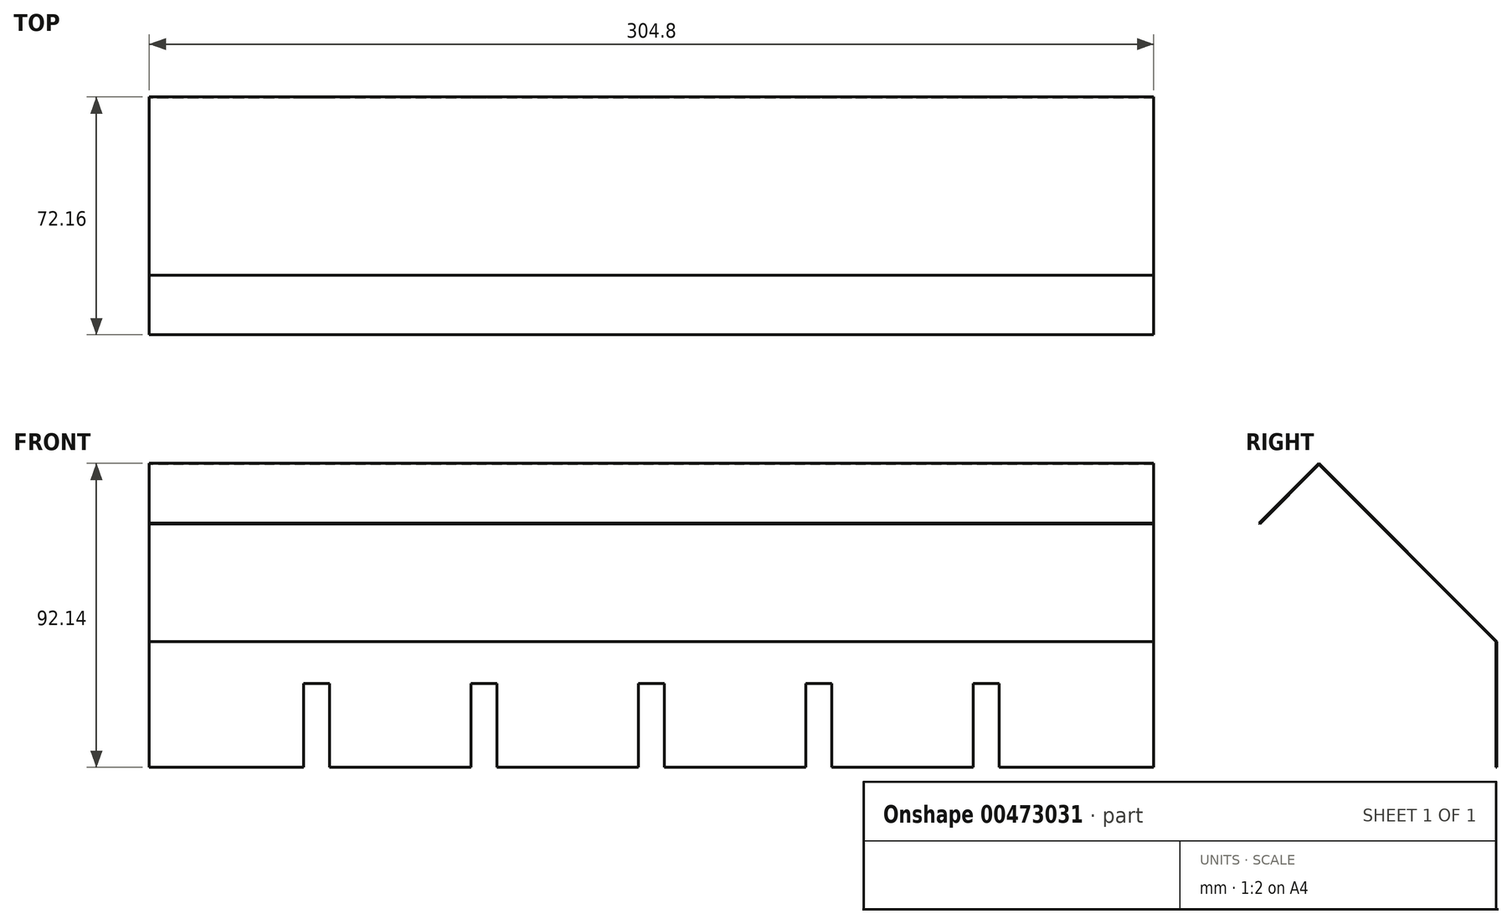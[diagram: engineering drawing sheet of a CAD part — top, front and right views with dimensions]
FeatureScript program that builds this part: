
annotation { "Feature Type Name" : "Feature", "Feature Type Description" : "" }
export const myFeature = defineFeature(function(context is Context, id is Id, definition is map)
    precondition{}
    {
        {
            var Q0;
            Q0=qCreatedBy(makeId("Front.planeOp"),FACE);
            var sketch = newSketch(context, id + "F0", { "sketchPlane" : qUnion([Q0])});
            skLineSegment(sketch, "E0.top", {"start": v(152.4, -50.8) * mm, "end": v(105.56, -50.8) * mm});
            skLineSegment(sketch, "E0.left", {"start": v(152.4, -12.7) * mm, "end": v(152.4, -50.8) * mm});
            skLineSegment(sketch, "E0.right", {"start": v(-152.4, -12.7) * mm, "end": v(-152.4, -50.8) * mm});
            skPoint(sketch, "E0.middle", {"position": v(0, 0) * mm});
            skLineSegment(sketch, "E1.0", {"start": v(105.56, -25.4) * mm, "end": v(97.64, -25.4) * mm});
            skLineSegment(sketch, "E2.0", {"start": v(-105.57, -25.4) * mm, "end": v(-105.57, -50.8) * mm});
            skLineSegment(sketch, "E3.0", {"start": v(-97.64, -25.4) * mm, "end": v(-97.64, -50.8) * mm});
            skLineSegment(sketch, "E4.0", {"start": v(-54.76, -25.4) * mm, "end": v(-54.76, -50.8) * mm});
            skLineSegment(sketch, "E5.0", {"start": v(-3.96, -25.4) * mm, "end": v(-3.96, -50.8) * mm});
            skLineSegment(sketch, "E6.0", {"start": v(3.96, -25.4) * mm, "end": v(3.96, -50.8) * mm});
            skLineSegment(sketch, "E7.0", {"start": v(46.84, -25.4) * mm, "end": v(46.84, -50.8) * mm});
            skLineSegment(sketch, "E8.0", {"start": v(54.76, -25.4) * mm, "end": v(54.76, -50.8) * mm});
            skLineSegment(sketch, "E9.0", {"start": v(97.64, -25.4) * mm, "end": v(97.64, -50.8) * mm});
            skLineSegment(sketch, "E10.0", {"start": v(105.56, -25.4) * mm, "end": v(105.56, -50.8) * mm});
            skLineSegment(sketch, "E11.0", {"start": v(-46.83, -25.4) * mm, "end": v(-46.83, -50.8) * mm});
            skLineSegment(sketch, "E12.trimOffspring", {"start": v(-105.57, -50.8) * mm, "end": v(-152.4, -50.8) * mm});
            skLineSegment(sketch, "E13.trimOffspring", {"start": v(-97.64, -25.4) * mm, "end": v(-105.57, -25.4) * mm});
            skLineSegment(sketch, "E14.trimOffspring", {"start": v(-54.76, -50.8) * mm, "end": v(-97.64, -50.8) * mm});
            skLineSegment(sketch, "E15.trimOffspring", {"start": v(-3.96, -50.8) * mm, "end": v(-46.83, -50.8) * mm});
            skLineSegment(sketch, "E16.trimOffspring", {"start": v(46.84, -50.8) * mm, "end": v(3.96, -50.8) * mm});
            skLineSegment(sketch, "E17.trimOffspring", {"start": v(97.64, -50.8) * mm, "end": v(54.76, -50.8) * mm});
            skLineSegment(sketch, "E18.trimOffspring", {"start": v(54.76, -25.4) * mm, "end": v(46.84, -25.4) * mm});
            skLineSegment(sketch, "E19.trimOffspring", {"start": v(3.96, -25.4) * mm, "end": v(-3.96, -25.4) * mm});
            skLineSegment(sketch, "E20.trimOffspring", {"start": v(-46.83, -25.4) * mm, "end": v(-54.76, -25.4) * mm});
            skLineSegment(sketch, "E21.0", {"start": v(152.4, -12.7) * mm, "end": v(-152.4, -12.7) * mm});
            skSolve(sketch);
        }
        {
            var Q0;
            Q0=makeQuery(id+"F0.imprint","IMPRINT",FACE,{"disambiguationData":[TD([[makeQuery(id+"F0.imprint","IMPRINT",EDGE,{"derivedFrom":sQuery(id+"F0.wireOp",EDGE,"E0.top")}),-1.0]])]});
            extrude(context, id + "F1", {"entities" : qUnion([Q0]), "depth" : 0.32 * mm});
        }
        {
            var Q0;
            Q0=makeQuery(id+"F1.opExtrude","SWEPT_FACE",FACE,{"disambiguationData":[OSD([sQuery(id+"F0.wireOp",EDGE,"E0.right")])]});
            var sketch = newSketch(context, id + "F2", { "sketchPlane" : qUnion([Q0])});
            skLineSegment(sketch, "E22", {"start": v(0.32, -12.7) * mm, "end": v(54.2, 41.18) * mm});
            skLineSegment(sketch, "E23", {"start": v(0, -12.7) * mm, "end": v(54.04, 41.34) * mm});
            skLineSegment(sketch, "E24", {"start": v(54.04, 41.34) * mm, "end": v(54.2, 41.18) * mm});
            skSolve(sketch);
        }
        {
            var Q0;
            Q0=makeQuery(id+"F2.imprint","IMPRINT",FACE,{"disambiguationData":[TD([[makeQuery(id+"F2.imprint","IMPRINT",EDGE,{"derivedFrom":sQuery(id+"F2.wireOp",EDGE,"E22")}),1.0]])]});
            extrude(context, id + "F3", {"entities" : qUnion([Q0]), "operationType" : NewBodyOperationType.ADD, "oppositeDirection" : true, "depth" : 304.8 * mm});
        }
        {
            var Q0;
            {var subQ0=sQuery(id+"F0.wireOp",EDGE,"E0.right");Q0=makeQuery(id+"F3.boolean.opBoolean","MERGE",FACE,{"derivedFrom":[makeQuery(id+"F1.opExtrude","SWEPT_FACE",FACE,{"disambiguationData":[OSD([subQ0])]}),makeQuery(id+"F3.opExtrude","CAP_FACE",FACE,{"disambiguationData":[OSD([subQ0,sQuery(id+"F0.wireOp",EDGE,"E21.0"),sQuery(id+"F2.wireOp",EDGE,"E22"),sQuery(id+"F2.wireOp",EDGE,"E23"),sQuery(id+"F2.wireOp",EDGE,"E24")])],"isStart":true})]});}
            var sketch = newSketch(context, id + "F4", { "sketchPlane" : qUnion([Q0])});
            skLineSegment(sketch, "E25", {"start": v(54.2, 41.18) * mm, "end": v(72.16, 23.22) * mm});
            skLineSegment(sketch, "E26", {"start": v(72.16, 23.22) * mm, "end": v(71.94, 23) * mm});
            skLineSegment(sketch, "E27", {"start": v(71.94, 23) * mm, "end": v(53.97, 40.96) * mm});
            skSolve(sketch);
        }
        {
            var Q0;
            {var subQ0=sQuery(id+"F4.wireOp",EDGE,"E25");Q0=makeQuery(id+"F4.imprint","IMPRINT",FACE,{"disambiguationData":[TD([[makeQuery(id+"F4.imprint","IMPRINT",EDGE,{"derivedFrom":subQ0}),-1.0]])]});}
            extrude(context, id + "F5", {"entities" : qUnion([Q0]), "operationType" : NewBodyOperationType.ADD, "oppositeDirection" : true, "depth" : 304.8 * mm});
        }
    });
